# Revit family: Shower-Return_Panel-KOHLER-COMPOSED-1.1922.041_1
name_source: partatom
category: Specialty Equipment
revit_build: Autodesk Revit 2017 (Build: 20160225_1515(x64)
units: mm (PartAtom-declared; Revit-internal decimal feet)

## family parameters
Cut with Voids When Loaded = No
Host = Face
OmniClass Number = 23.31.17.17
OmniClass Title = Shower Enclosures
Part Type = Normal
Room Calculation Point = No
Round Connector Dimension = Use Diameter
Shared = No

## types (1)
- Polished Chrome
    ADA Compliant = No
    Assembly Code = C1030200
    Date Modified = 10/18/2021
    Default Elevation = 4"
    Description = Hinged Return Panel 400
    Finish = Kohler-Metal-CP-Polished_Chrome
    Height = 78 3/4"
    Length = 1"
    Manufacturer = KOHLER Co.
    Master Format 2014 = 10 28 19.16
    Master Format 2014 Name = Shower Doors
    Material = Premium Metal Construction
    Model = 1.1922.041
    Product Name = COMPOSED
    Type = 1
    URL = https://www.kohler.co.uk
    WaterSense Certified = No
    Width = 18 3/16"

## geometry (parser evidence)
native form markers: Sweep x3
no freeform markers — native parametric forms only
